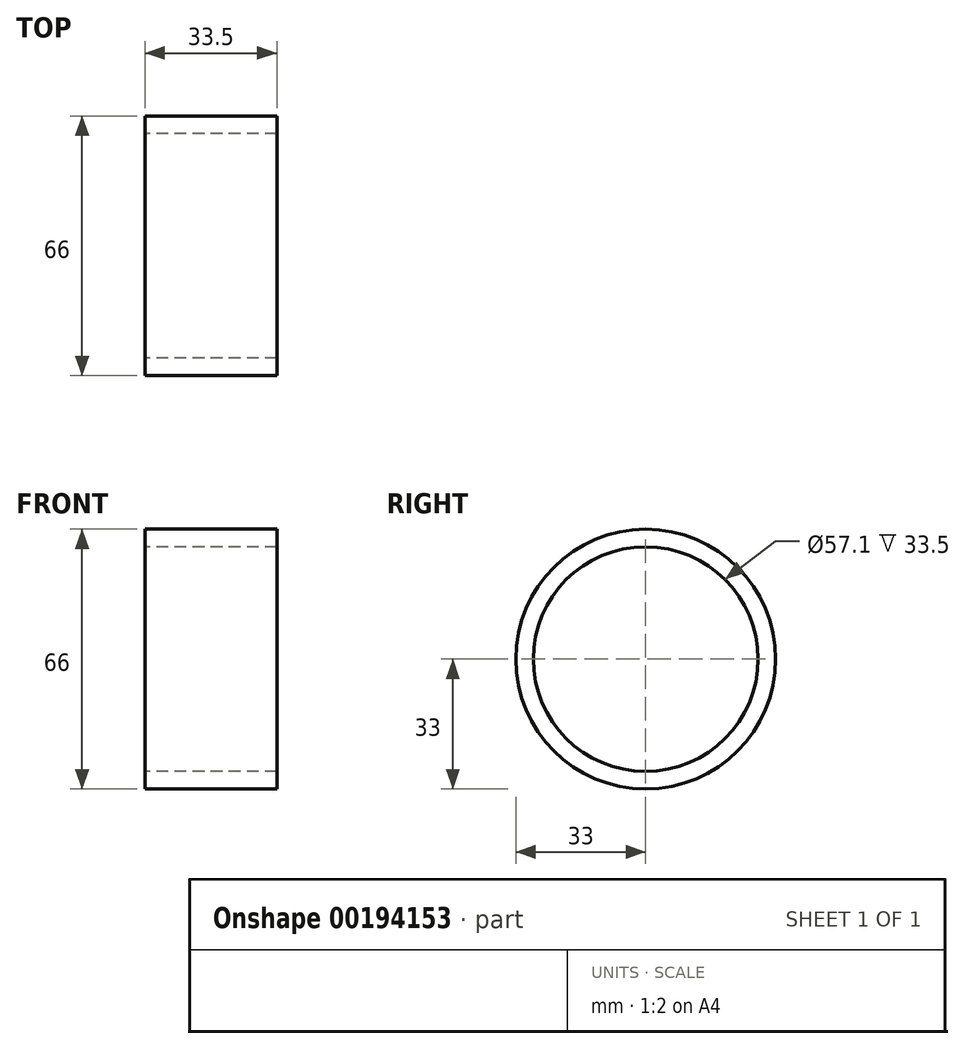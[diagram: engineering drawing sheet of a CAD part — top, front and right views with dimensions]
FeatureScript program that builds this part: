
annotation { "Feature Type Name" : "Feature", "Feature Type Description" : "" }
export const myFeature = defineFeature(function(context is Context, id is Id, definition is map)
    precondition{}
    {
        {
            var Q0;
            Q0=qCreatedBy(makeId("Right.planeOp"),FACE);
            var sketch = newSketch(context, id + "F0", { "sketchPlane" : qUnion([Q0])});
            skCircle(sketch, "E0", {"center": v(0, 0) * mm, "radius": 28.55 * mm});
            skCircle(sketch, "E1", {"center": v(0, 0) * mm, "radius": 33 * mm});
            skSolve(sketch);
        }
        {
            var Q0;
            Q0 = qSketchRegion(id + "F0", true);
            extrude(context, id + "F1", {"entities" : qUnion([Q0]), "depth" : (25 + 8.5) * mm});
        }
    });
